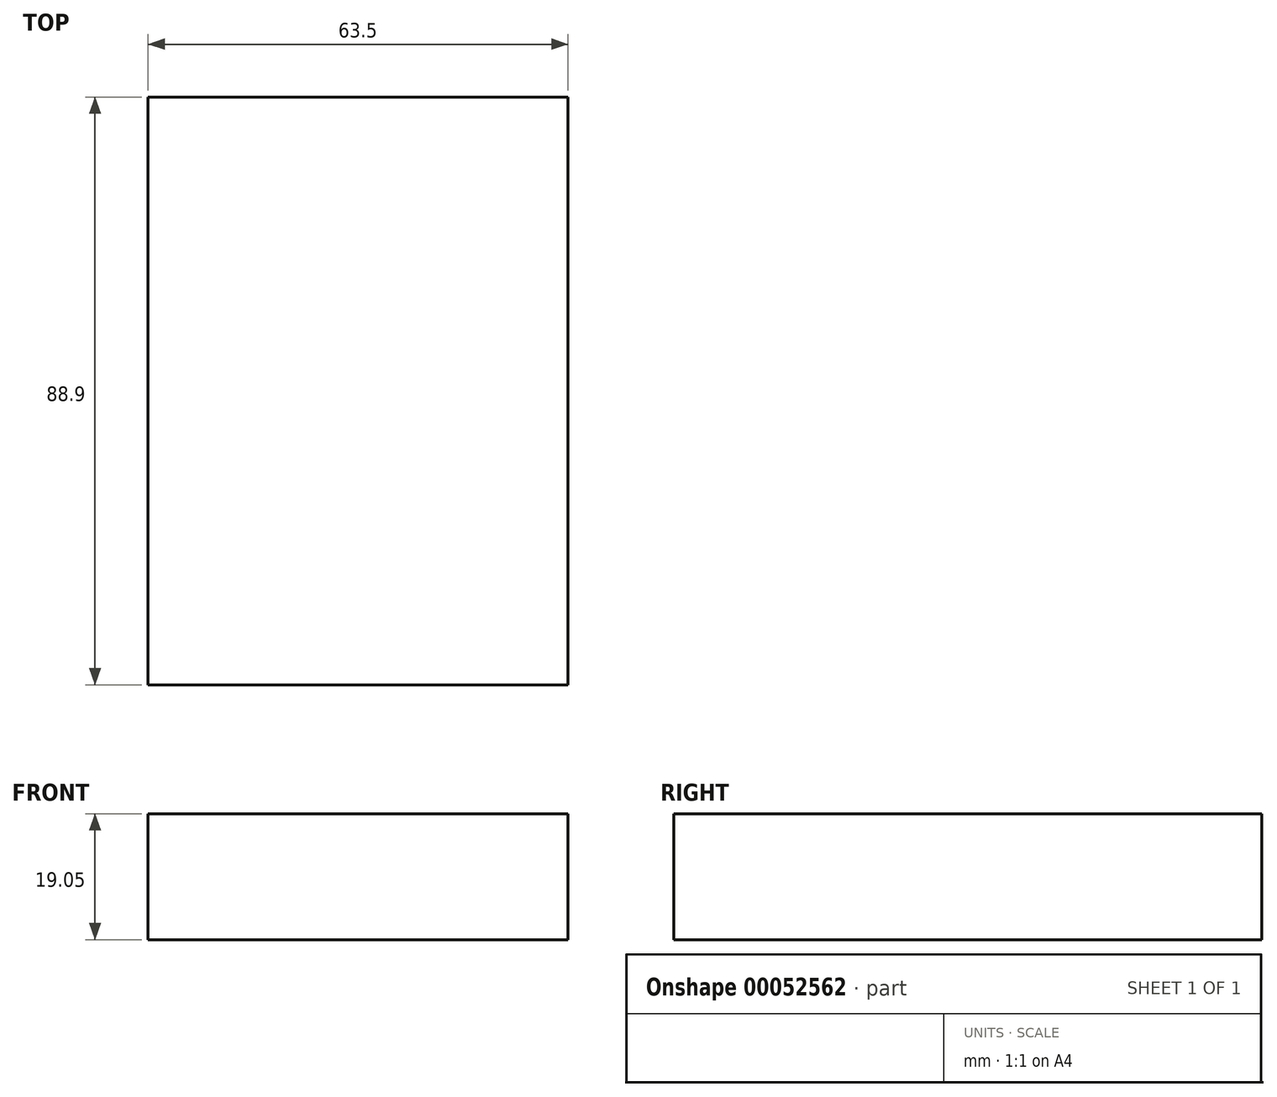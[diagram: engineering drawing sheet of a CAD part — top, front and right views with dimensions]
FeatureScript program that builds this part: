
annotation { "Feature Type Name" : "Feature", "Feature Type Description" : "" }
export const myFeature = defineFeature(function(context is Context, id is Id, definition is map)
    precondition{}
    {
        {
            var Q0;
            Q0=qCreatedBy(makeId("Top.planeOp"),FACE);
            var sketch = newSketch(context, id + "F0", { "sketchPlane" : qUnion([Q0])});
            skLineSegment(sketch, "E0.rect.bottom", {"start": v(31.75, 44.45) * mm, "end": v(-31.75, 44.45) * mm});
            skLineSegment(sketch, "E0.rect.top", {"start": v(31.75, -44.45) * mm, "end": v(-31.75, -44.45) * mm});
            skLineSegment(sketch, "E0.rect.left", {"start": v(31.75, 44.45) * mm, "end": v(31.75, -44.45) * mm});
            skLineSegment(sketch, "E0.rect.right", {"start": v(-31.75, 44.45) * mm, "end": v(-31.75, -44.45) * mm});
            skPoint(sketch, "E0.rect.middle", {"position": v(0, 0) * mm});
            skSolve(sketch);
        }
        {
            var Q0;
            Q0=makeQuery(id+"F0.imprint","IMPRINT",FACE,{"disambiguationData":[TD([[makeQuery(id+"F0.imprint","IMPRINT",EDGE,{"derivedFrom":sQuery(id+"F0.wireOp",EDGE,"E0.rect.bottom")}),1.0]])]});
            extrude(context, id + "F1", {"entities" : qUnion([Q0]), "depth" : 19.05 * mm});
        }
    });
